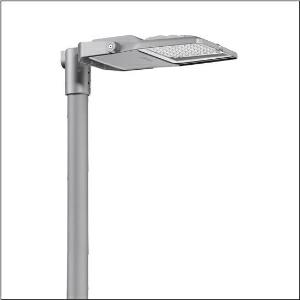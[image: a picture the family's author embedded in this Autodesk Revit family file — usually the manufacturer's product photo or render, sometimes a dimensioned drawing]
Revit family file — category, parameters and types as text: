
# Revit family: floodlight_fl_21_iq_mini___pl64_5xa7771b4e3a_3408
name_source: partatom
category: Lighting Fixtures
units: mm (PartAtom-declared; Revit-internal decimal feet)

## family parameters
Cut with Voids When Loaded = No
Host = Face
Light Source = No
Part Type = Normal
Room Calculation Point = No
Round Connector Dimension = Use Diameter
Shared = No

## types (1)
- --- (1 x LED, 6270 lm, 45.5 W, 4000K)
    Apparent Load = 46 VA
    CIE Flux Codes = 28 80 98 100 100
    Color Rendering = 70
    Color Temperature = 4000K
    Default Elevation = 1800 mm
    Description = Floodlight FL 21 iQ mini, floodlight, primary light control with lens, of PMMA, primary optical cover: protective disc, of toughened safety glass, transparent, light distribution: PL64, light emission: direct distribution, installation type: surface-mounted, LED, High Power LED, rated luminous flux: 6.270lm, luminous efficacy: 138lm/W, light colour: 740, colour temperature: 4000K, control: Auto-Match, Temp-Guard, Lumen-Switch, Night-Set, Smart-Wire, Light-Fading, Desk-Remote (wireless, voltage-free reading and setting of iQ features in the workshop via application-optimized NFC function/RFID function), optimised constant luminous flux control (CLO 2.0), with terminal, 6-pole, mains connection: 220..240V, AC, 50/60Hz, start of lifetime: 46W, end of service life: 48W, reduction: 22W, luminaire housing, of diecast aluminium, powder-coated, Siteco® metallic grey (DB 702S), corrosivity category C5 mid according to DIN EN ISO 12944, sealing non-destructively replaceable, please order mast flange separately, mast bracket, of steel, galvanised, powder-coated, Siteco® metallic grey (DB 702S), protection rating (complete): IP66, insulation class (complete): insulation class II (safety insulation), certification: CE, ENEC, VDE, protection symbol: D, impact resistance: IK08, permissible operating ambient temperature: -40..+40°C, permissible operating ambient temperature for outdoor applications: -40..+50°C, standard: DIN EN 12944, LABS conformity tested according to VDMA 24364:2018-05, packaging unit: 1 piece

Light Distribution: PL64
    Height = 70 mm
    Lamp = 1 x LED
    Lamp Light Flux = 6270 lm
    Lamp Power = 45.5 W
    Lamp count = 1
    Length = 485 mm
    Luminous efficacy = 138 lm/W
    Manufacturer = Siteco
    ModVariant = No
    Model = 5XA7771B4E3A
    Number of Poles = 1
    OnlyDefault = Yes
    Power Factor = 1
    Product Name = Floodlight FL 21 iQ mini | PL64
    Product group = floodlight | pylon annexe
    ProductGroupID = 6200
    Protection Class = Protection class II
    Protection Degree = IP 66
    RLX_Detail_Level = 1
    RLX_Emergency_Light_Flux = 0 lm
    RLX_Emergency_Type = 0
    RLX_Emergency_Type_DB = No
    RlxData = <blob elided: 101101 chars, md5=492b9aae>
    Socket = socket
    Standby Power = 0 W
    System Light Flux = 6270 lm
    System Power = 46 W
    Type Comments = factory setting: luminous flux: 100 % | dim-lin: 254 | 463 mA
    Type Image = l_1007125.jpg
    URL = http://relux.com
    VarID = @adj_099345
    Voltage = 0 V
    Weight = 0.00 kg
    Width = 337 mm

## geometry (parser evidence)
native form markers: Blend x4, Sweep x13
no freeform markers — native parametric forms only
